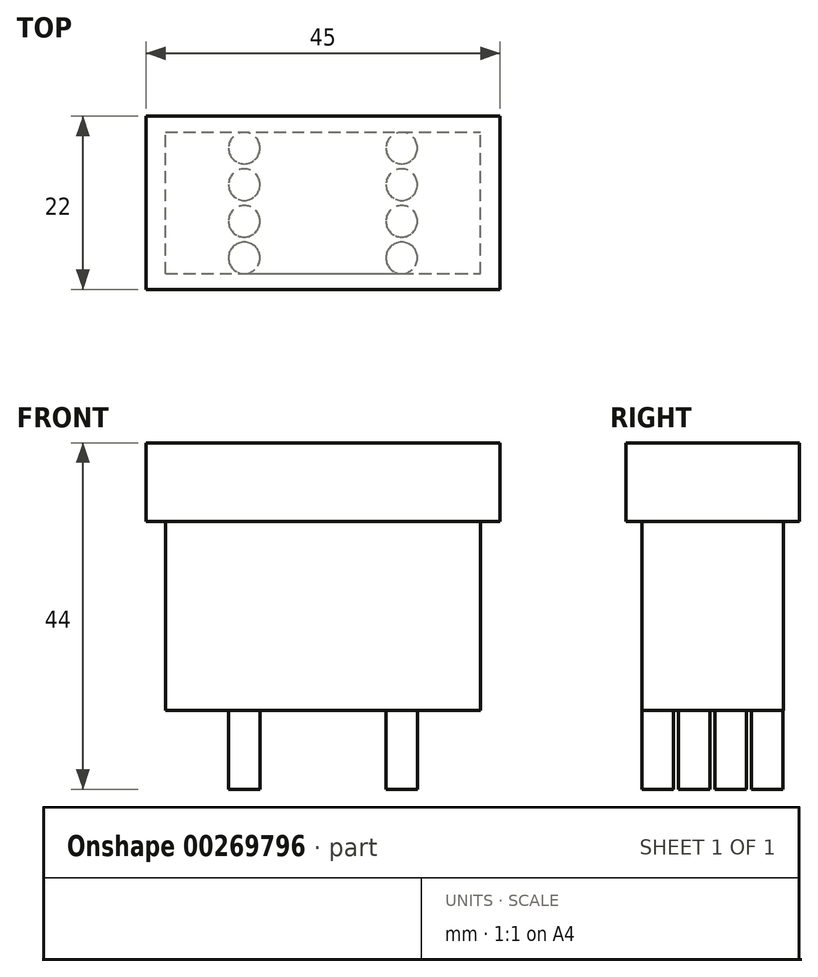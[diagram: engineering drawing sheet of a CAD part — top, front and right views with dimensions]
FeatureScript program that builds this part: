
annotation { "Feature Type Name" : "Feature", "Feature Type Description" : "" }
export const myFeature = defineFeature(function(context is Context, id is Id, definition is map)
    precondition{}
    {
        {
            var Q0;
            Q0=qCreatedBy(makeId("Top.planeOp"),FACE);
            var sketch = newSketch(context, id + "F0", { "sketchPlane" : qUnion([Q0])});
            skLineSegment(sketch, "E0.bottom", {"start": v(-56.31, -18.46) * mm, "end": v(-16.31, -18.46) * mm});
            skLineSegment(sketch, "E0.top", {"start": v(-56.31, -0.46) * mm, "end": v(-16.31, -0.46) * mm});
            skLineSegment(sketch, "E0.left", {"start": v(-56.31, -18.46) * mm, "end": v(-56.31, -0.46) * mm});
            skLineSegment(sketch, "E0.right", {"start": v(-16.31, -18.46) * mm, "end": v(-16.31, -0.46) * mm});
            skLineSegment(sketch, "E1.bottom", {"start": v(-58.81, -20.46) * mm, "end": v(-13.81, -20.46) * mm});
            skLineSegment(sketch, "E1.top", {"start": v(-58.81, 1.54) * mm, "end": v(-13.81, 1.54) * mm});
            skLineSegment(sketch, "E1.left", {"start": v(-58.81, -20.46) * mm, "end": v(-58.81, 1.54) * mm});
            skLineSegment(sketch, "E1.right", {"start": v(-13.81, -20.46) * mm, "end": v(-13.81, 1.54) * mm});
            skSolve(sketch);
        }
        {
            var Q0;
            Q0=makeQuery(id+"F0.imprint","IMPRINT",FACE,{"disambiguationData":[TD([[makeQuery(id+"F0.imprint","IMPRINT",EDGE,{"derivedFrom":sQuery(id+"F0.wireOp",EDGE,"E0.bottom")}),-1.0]])]});
            var Q1;
            Q1=makeQuery(id+"F0.imprint","IMPRINT",FACE,{"disambiguationData":[TD([[makeQuery(id+"F0.imprint","IMPRINT",EDGE,{"derivedFrom":sQuery(id+"F0.wireOp",EDGE,"E0.bottom")}),1.0]])]});
            extrude(context, id + "F1", {"entities" : qUnion([Q0, Q1]), "depth" : 10 * mm});
        }
        {
            var Q0;
            Q0=makeQuery(id+"F0.imprint","IMPRINT",FACE,{"disambiguationData":[TD([[makeQuery(id+"F0.imprint","IMPRINT",EDGE,{"derivedFrom":sQuery(id+"F0.wireOp",EDGE,"E0.bottom")}),1.0]])]});
            extrude(context, id + "F2", {"entities" : qUnion([Q0]), "operationType" : NewBodyOperationType.ADD, "oppositeDirection" : true, "depth" : 24 * mm});
        }
        {
            var Q0;
            Q0=makeQuery(id+"F2.opExtrude","CAP_FACE",FACE,{"disambiguationData":[OSD([sQuery(id+"F0.wireOp",EDGE,"E0.bottom"),sQuery(id+"F0.wireOp",EDGE,"E0.top"),sQuery(id+"F0.wireOp",EDGE,"E0.left"),sQuery(id+"F0.wireOp",EDGE,"E0.right")])],"isStart":false});
            var sketch = newSketch(context, id + "F3", { "sketchPlane" : qUnion([Q0])});
            skLineSegment(sketch, "E2", {"start": v(-46.31, -23.1) * mm, "end": v(-46.31, 42) * mm, "construction": true});
            skLineSegment(sketch, "E3", {"start": v(-26.31, -8.65) * mm, "end": v(-26.31, 38.17) * mm, "construction": true});
            skPoint(sketch, "E4", {"position": v(-46.31, 16.46) * mm});
            skCircle(sketch, "E5", {"center": v(-46.31, 16.46) * mm, "radius": 2 * mm});
            skCircle(sketch, "E6.0.1.0", {"center": v(-46.31, 11.8) * mm, "radius": 2 * mm});
            skCircle(sketch, "E6.0.2.0", {"center": v(-46.31, 7.16) * mm, "radius": 2 * mm});
            skCircle(sketch, "E6.0.3.0", {"center": v(-46.31, 2.5) * mm, "radius": 2 * mm});
            skCircle(sketch, "E6.1.0.0", {"center": v(-26.31, 16.46) * mm, "radius": 2 * mm});
            skCircle(sketch, "E6.1.1.0", {"center": v(-26.31, 11.8) * mm, "radius": 2 * mm});
            skCircle(sketch, "E6.1.2.0", {"center": v(-26.31, 7.16) * mm, "radius": 2 * mm});
            skCircle(sketch, "E6.1.3.0", {"center": v(-26.31, 2.5) * mm, "radius": 2 * mm});
            skLineSegment(sketch, "E6.direction1", {"start": v(-46.31, 16.46) * mm, "end": v(-26.31, 16.46) * mm, "construction": true});
            skLineSegment(sketch, "E6.direction2", {"start": v(-46.31, 16.46) * mm, "end": v(-46.31, 11.8) * mm, "construction": true});
            skSolve(sketch);
        }
        {
            var Q0;
            Q0 = qSketchRegion(id + "F3", true);
            extrude(context, id + "F4", {"entities" : qUnion([Q0]), "operationType" : NewBodyOperationType.ADD, "depth" : 10 * mm});
        }
    });
